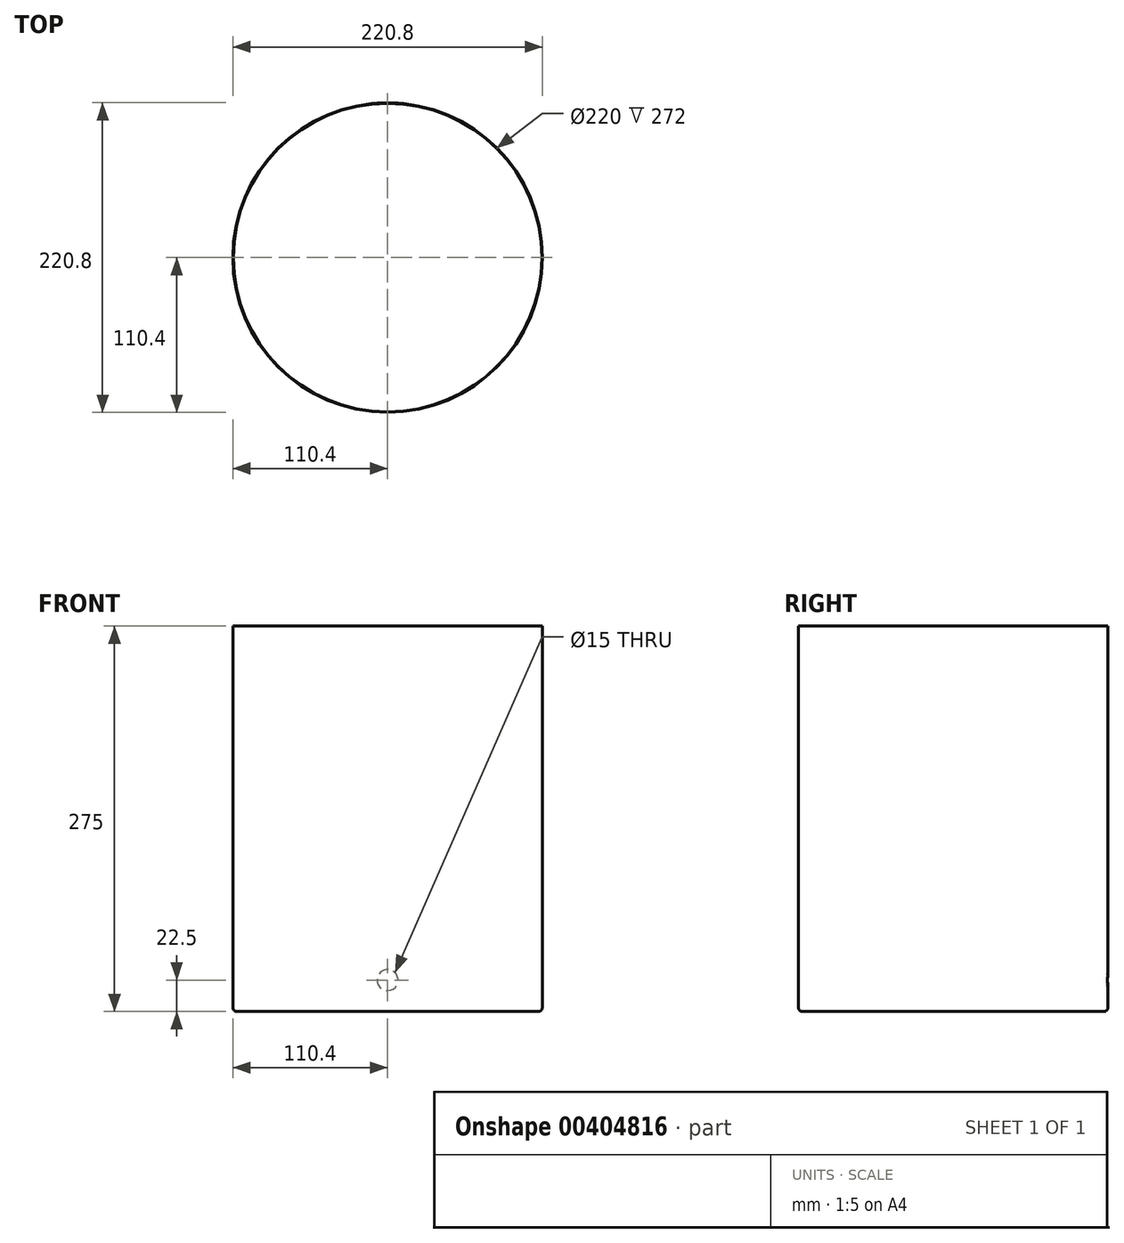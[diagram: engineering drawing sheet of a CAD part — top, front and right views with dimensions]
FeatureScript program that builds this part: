
annotation { "Feature Type Name" : "Feature", "Feature Type Description" : "" }
export const myFeature = defineFeature(function(context is Context, id is Id, definition is map)
    precondition{}
    {
        {
            var Q0;
            Q0=qCreatedBy(makeId("Front.planeOp"),FACE);
            var sketch = newSketch(context, id + "F0", { "sketchPlane" : qUnion([Q0])});
            skLineSegment(sketch, "E0", {"start": v(0, 0) * mm, "end": v(107.4, 0) * mm});
            skLineSegment(sketch, "E1", {"start": v(110.4, 3) * mm, "end": v(110.4, 275) * mm});
            skPoint(sketch, "E2.visualSharp", {"position": v(110.4, 0) * mm});
            skArc(sketch, "E2.filletArc", {"start": v(107.4, 0) * mm, "mid": v(109.53, 0.88) * mm, "end": v(110.4, 3) * mm});
            skLineSegment(sketch, "E3.0", {"start": v(110, 3) * mm, "end": v(110, 275) * mm});
            skArc(sketch, "E3.1", {"start": v(107.4, 0.4) * mm, "mid": v(109.24, 1.16) * mm, "end": v(110, 3) * mm});
            skLineSegment(sketch, "E3.2", {"start": v(0, 0.4) * mm, "end": v(107.4, 0.4) * mm});
            skLineSegment(sketch, "E4", {"start": v(0, 0.4) * mm, "end": v(0, 0) * mm});
            skLineSegment(sketch, "E5", {"start": v(110.4, 275) * mm, "end": v(110, 275) * mm});
            skSolve(sketch);
        }
        {
            var Q0;
            Q0=makeQuery(id+"F0.imprint","IMPRINT",FACE,{"disambiguationData":[TD([[makeQuery(id+"F0.imprint","IMPRINT",EDGE,{"derivedFrom":sQuery(id+"F0.wireOp",EDGE,"E0")}),1.0]])]});
            var Q1;
            Q1=sQuery(id+"F0.wireOp",EDGE,"E4");
            revolve(context, id + "F1", {"entities" : qUnion([Q0]), "axis" : qUnion([Q1]), "revolveType" : RevolveType.FULL});
        }
        {
            var Q0;
            Q0=qCreatedBy(makeId("Front.planeOp"),FACE);
            var sketch = newSketch(context, id + "F2", { "sketchPlane" : qUnion([Q0])});
            skCircle(sketch, "E6", {"center": v(0, 22.5) * mm, "radius": 7.5 * mm});
            skSolve(sketch);
        }
        {
            var Q0;
            Q0 = qSketchRegion(id + "F2", true);
            extrude(context, id + "F3", {"entities" : qUnion([Q0]), "operationType" : NewBodyOperationType.REMOVE, "oppositeDirection" : true, "depth" : 226.06 * mm});
        }
    });
